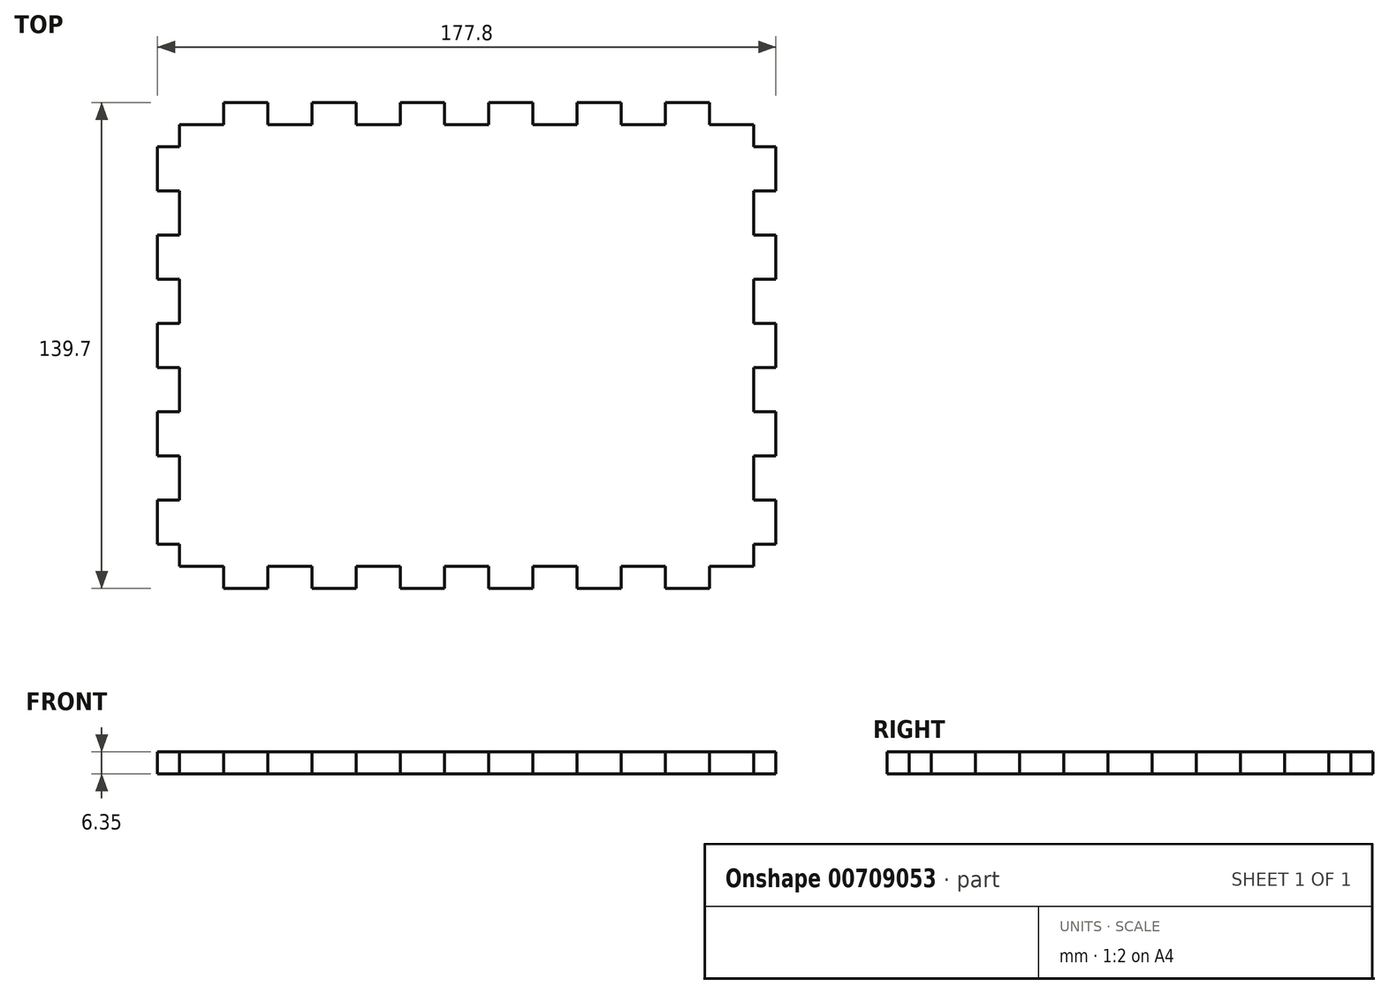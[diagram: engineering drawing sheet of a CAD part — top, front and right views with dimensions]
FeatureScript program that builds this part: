
annotation { "Feature Type Name" : "Feature", "Feature Type Description" : "" }
export const myFeature = defineFeature(function(context is Context, id is Id, definition is map)
    precondition{}
    {
        {
            var Q0;
            Q0=qCreatedBy(makeId("Top.planeOp"),FACE);
            var sketch = newSketch(context, id + "F0", { "sketchPlane" : qUnion([Q0])});
            skLineSegment(sketch, "E0.bottom", {"start": v(19.05, 0) * mm, "end": v(31.75, 0) * mm});
            skLineSegment(sketch, "E0.left", {"start": v(0, -12.7) * mm, "end": v(0, -25.4) * mm});
            skLineSegment(sketch, "E1", {"start": v(6.35, -6.35) * mm, "end": v(19.05, -6.35) * mm});
            skLineSegment(sketch, "E2", {"start": v(19.05, -6.35) * mm, "end": v(19.05, 0) * mm});
            skLineSegment(sketch, "E3", {"start": v(31.75, 0) * mm, "end": v(31.75, -6.35) * mm});
            skLineSegment(sketch, "E4", {"start": v(31.75, -6.35) * mm, "end": v(44.45, -6.35) * mm});
            skLineSegment(sketch, "E5", {"start": v(44.45, -6.35) * mm, "end": v(44.45, 0) * mm});
            skLineSegment(sketch, "E6", {"start": v(44.45, 0) * mm, "end": v(57.15, 0) * mm});
            skLineSegment(sketch, "E7", {"start": v(57.15, 0) * mm, "end": v(57.15, -6.35) * mm});
            skLineSegment(sketch, "E8", {"start": v(57.15, -6.35) * mm, "end": v(69.85, -6.35) * mm});
            skLineSegment(sketch, "E9", {"start": v(69.85, -6.35) * mm, "end": v(69.85, 0) * mm});
            skLineSegment(sketch, "E10", {"start": v(69.85, 0) * mm, "end": v(82.55, 0) * mm});
            skLineSegment(sketch, "E11", {"start": v(82.55, 0) * mm, "end": v(82.55, -6.35) * mm});
            skLineSegment(sketch, "E12", {"start": v(82.55, -6.35) * mm, "end": v(95.25, -6.35) * mm});
            skLineSegment(sketch, "E13", {"start": v(95.25, -6.35) * mm, "end": v(95.25, 0) * mm});
            skLineSegment(sketch, "E14.trimOffspring", {"start": v(95.25, 0) * mm, "end": v(107.95, 0) * mm});
            skLineSegment(sketch, "E15", {"start": v(107.95, 0) * mm, "end": v(107.95, -6.35) * mm});
            skLineSegment(sketch, "E16", {"start": v(107.95, -6.35) * mm, "end": v(120.65, -6.35) * mm});
            skLineSegment(sketch, "E17", {"start": v(120.65, -6.35) * mm, "end": v(120.65, 0) * mm});
            skLineSegment(sketch, "E18", {"start": v(120.65, 0) * mm, "end": v(133.35, 0) * mm});
            skLineSegment(sketch, "E19", {"start": v(133.35, 0) * mm, "end": v(133.35, -6.35) * mm});
            skLineSegment(sketch, "E20", {"start": v(133.35, -6.35) * mm, "end": v(146.05, -6.35) * mm});
            skLineSegment(sketch, "E21", {"start": v(146.05, -6.35) * mm, "end": v(146.05, 0) * mm});
            skLineSegment(sketch, "E22", {"start": v(146.05, 0) * mm, "end": v(158.75, 0) * mm});
            skLineSegment(sketch, "E23", {"start": v(158.75, 0) * mm, "end": v(158.75, -6.35) * mm});
            skLineSegment(sketch, "E24", {"start": v(158.75, -6.35) * mm, "end": v(171.45, -6.35) * mm});
            skPoint(sketch, "E25.orphan", {"position": v(0, 0) * mm});
            skPoint(sketch, "E26.orphan", {"position": v(177.8, 0) * mm});
            skLineSegment(sketch, "E27", {"start": v(6.35, -6.35) * mm, "end": v(6.35, -12.7) * mm});
            skLineSegment(sketch, "E28", {"start": v(6.35, -12.7) * mm, "end": v(0, -12.7) * mm});
            skLineSegment(sketch, "E29", {"start": v(0, -25.4) * mm, "end": v(6.35, -25.4) * mm});
            skLineSegment(sketch, "E30", {"start": v(6.35, -25.4) * mm, "end": v(6.35, -38.1) * mm});
            skLineSegment(sketch, "E31", {"start": v(6.35, -38.1) * mm, "end": v(0, -38.1) * mm});
            skLineSegment(sketch, "E32", {"start": v(0, -38.1) * mm, "end": v(0, -50.8) * mm});
            skLineSegment(sketch, "E33", {"start": v(0, -50.8) * mm, "end": v(6.35, -50.8) * mm});
            skLineSegment(sketch, "E34", {"start": v(6.35, -50.8) * mm, "end": v(6.35, -63.5) * mm});
            skLineSegment(sketch, "E35", {"start": v(6.35, -63.5) * mm, "end": v(0, -63.5) * mm});
            skLineSegment(sketch, "E36.trimOffspring", {"start": v(0, -63.5) * mm, "end": v(0, -76.2) * mm});
            skLineSegment(sketch, "E37", {"start": v(0, -76.2) * mm, "end": v(6.35, -76.2) * mm});
            skLineSegment(sketch, "E38", {"start": v(6.35, -76.2) * mm, "end": v(6.35, -88.9) * mm});
            skLineSegment(sketch, "E39", {"start": v(6.35, -88.9) * mm, "end": v(0, -88.9) * mm});
            skLineSegment(sketch, "E40", {"start": v(0, -88.9) * mm, "end": v(0, -101.6) * mm});
            skLineSegment(sketch, "E41", {"start": v(0, -101.6) * mm, "end": v(6.35, -101.6) * mm});
            skLineSegment(sketch, "E42", {"start": v(6.35, -101.6) * mm, "end": v(6.35, -114.3) * mm});
            skLineSegment(sketch, "E43", {"start": v(6.35, -114.3) * mm, "end": v(0, -114.3) * mm});
            skLineSegment(sketch, "E44", {"start": v(0, -114.3) * mm, "end": v(0, -127) * mm});
            skLineSegment(sketch, "E45", {"start": v(0, -127) * mm, "end": v(6.35, -127) * mm});
            skLineSegment(sketch, "E46", {"start": v(6.35, -127) * mm, "end": v(6.35, -133.35) * mm});
            skLineSegment(sketch, "E47", {"start": v(88.9, -6.35) * mm, "end": v(88.9, -42.33) * mm, "construction": true});
            skLineSegment(sketch, "E48.MirrorCS", {"start": v(171.45, -6.35) * mm, "end": v(171.45, -12.7) * mm});
            skLineSegment(sketch, "E49.MirrorCS", {"start": v(171.45, -12.7) * mm, "end": v(177.8, -12.7) * mm});
            skLineSegment(sketch, "E50.MirrorCS", {"start": v(177.8, -12.7) * mm, "end": v(177.8, -25.4) * mm});
            skLineSegment(sketch, "E51.MirrorCS", {"start": v(177.8, -25.4) * mm, "end": v(171.45, -25.4) * mm});
            skLineSegment(sketch, "E52.MirrorCS", {"start": v(171.45, -25.4) * mm, "end": v(171.45, -38.1) * mm});
            skLineSegment(sketch, "E53.MirrorCS", {"start": v(171.45, -38.1) * mm, "end": v(177.8, -38.1) * mm});
            skLineSegment(sketch, "E54.MirrorCS", {"start": v(177.8, -38.1) * mm, "end": v(177.8, -50.8) * mm});
            skLineSegment(sketch, "E55.MirrorCS", {"start": v(177.8, -50.8) * mm, "end": v(171.45, -50.8) * mm});
            skLineSegment(sketch, "E56.MirrorCS", {"start": v(171.45, -50.8) * mm, "end": v(171.45, -63.5) * mm});
            skLineSegment(sketch, "E57.MirrorCS", {"start": v(171.45, -63.5) * mm, "end": v(177.8, -63.5) * mm});
            skLineSegment(sketch, "E58.MirrorCS", {"start": v(177.8, -63.5) * mm, "end": v(177.8, -76.2) * mm});
            skLineSegment(sketch, "E59.MirrorCS", {"start": v(177.8, -76.2) * mm, "end": v(171.45, -76.2) * mm});
            skLineSegment(sketch, "E60.MirrorCS", {"start": v(171.45, -76.2) * mm, "end": v(171.45, -88.9) * mm});
            skLineSegment(sketch, "E61.MirrorCS", {"start": v(171.45, -88.9) * mm, "end": v(177.8, -88.9) * mm});
            skLineSegment(sketch, "E62.MirrorCS", {"start": v(177.8, -88.9) * mm, "end": v(177.8, -101.6) * mm});
            skLineSegment(sketch, "E63.MirrorCS", {"start": v(177.8, -101.6) * mm, "end": v(171.45, -101.6) * mm});
            skLineSegment(sketch, "E64.MirrorCS", {"start": v(171.45, -101.6) * mm, "end": v(171.45, -114.3) * mm});
            skLineSegment(sketch, "E65.MirrorCS", {"start": v(171.45, -114.3) * mm, "end": v(177.8, -114.3) * mm});
            skLineSegment(sketch, "E66.MirrorCS", {"start": v(177.8, -114.3) * mm, "end": v(177.8, -127) * mm});
            skLineSegment(sketch, "E67.MirrorCS", {"start": v(177.8, -127) * mm, "end": v(171.45, -127) * mm});
            skLineSegment(sketch, "E68.MirrorCS", {"start": v(171.45, -127) * mm, "end": v(171.45, -133.35) * mm});
            skLineSegment(sketch, "E69", {"start": v(0, -69.85) * mm, "end": v(50.8, -69.85) * mm, "construction": true});
            skLineSegment(sketch, "E70.MirrorCS", {"start": v(6.35, -133.35) * mm, "end": v(19.05, -133.35) * mm});
            skLineSegment(sketch, "E71.MirrorCS", {"start": v(19.05, -133.35) * mm, "end": v(19.05, -139.7) * mm});
            skLineSegment(sketch, "E72.MirrorCS", {"start": v(19.05, -139.7) * mm, "end": v(31.75, -139.7) * mm});
            skLineSegment(sketch, "E73.MirrorCS", {"start": v(31.75, -139.7) * mm, "end": v(31.75, -133.35) * mm});
            skLineSegment(sketch, "E74.MirrorCS", {"start": v(31.75, -133.35) * mm, "end": v(44.45, -133.35) * mm});
            skLineSegment(sketch, "E75.MirrorCS", {"start": v(44.45, -133.35) * mm, "end": v(44.45, -139.7) * mm});
            skLineSegment(sketch, "E76.MirrorCS", {"start": v(44.45, -139.7) * mm, "end": v(57.15, -139.7) * mm});
            skLineSegment(sketch, "E77.MirrorCS", {"start": v(57.15, -139.7) * mm, "end": v(57.15, -133.35) * mm});
            skLineSegment(sketch, "E78.MirrorCS", {"start": v(57.15, -133.35) * mm, "end": v(69.85, -133.35) * mm});
            skLineSegment(sketch, "E79.MirrorCS", {"start": v(69.85, -133.35) * mm, "end": v(69.85, -139.7) * mm});
            skLineSegment(sketch, "E80.MirrorCS", {"start": v(69.85, -139.7) * mm, "end": v(82.55, -139.7) * mm});
            skLineSegment(sketch, "E81.MirrorCS", {"start": v(82.55, -139.7) * mm, "end": v(82.55, -133.35) * mm});
            skLineSegment(sketch, "E82.MirrorCS", {"start": v(82.55, -133.35) * mm, "end": v(95.25, -133.35) * mm});
            skLineSegment(sketch, "E83.MirrorCS", {"start": v(95.25, -133.35) * mm, "end": v(95.25, -139.7) * mm});
            skLineSegment(sketch, "E84.MirrorCS", {"start": v(95.25, -139.7) * mm, "end": v(107.95, -139.7) * mm});
            skLineSegment(sketch, "E85.MirrorCS", {"start": v(107.95, -139.7) * mm, "end": v(107.95, -133.35) * mm});
            skLineSegment(sketch, "E86.MirrorCS", {"start": v(107.95, -133.35) * mm, "end": v(120.65, -133.35) * mm});
            skLineSegment(sketch, "E87.MirrorCS", {"start": v(120.65, -133.35) * mm, "end": v(120.65, -139.7) * mm});
            skLineSegment(sketch, "E88.MirrorCS", {"start": v(120.65, -139.7) * mm, "end": v(133.35, -139.7) * mm});
            skLineSegment(sketch, "E89.MirrorCS", {"start": v(133.35, -139.7) * mm, "end": v(133.35, -133.35) * mm});
            skLineSegment(sketch, "E90.MirrorCS", {"start": v(133.35, -133.35) * mm, "end": v(146.05, -133.35) * mm});
            skLineSegment(sketch, "E91.MirrorCS", {"start": v(146.05, -133.35) * mm, "end": v(146.05, -139.7) * mm});
            skLineSegment(sketch, "E92.MirrorCS", {"start": v(146.05, -139.7) * mm, "end": v(158.75, -139.7) * mm});
            skLineSegment(sketch, "E93.MirrorCS", {"start": v(158.75, -139.7) * mm, "end": v(158.75, -133.35) * mm});
            skLineSegment(sketch, "E94.MirrorCS", {"start": v(158.75, -133.35) * mm, "end": v(171.45, -133.35) * mm});
            skPoint(sketch, "E0.top.start.orphan", {"position": v(0, -139.7) * mm});
            skSolve(sketch);
        }
        {
            var Q0;
            Q0=makeQuery(id+"F0.imprint","IMPRINT",FACE,{"disambiguationData":[TD([[makeQuery(id+"F0.imprint","IMPRINT",EDGE,{"derivedFrom":sQuery(id+"F0.wireOp",EDGE,"E1")}),-1.0]])]});
            extrude(context, id + "F1", {"entities" : qUnion([Q0]), "depth" : 6.35 * mm, "offsetDistance" : 25.4 * mm});
        }
    });
